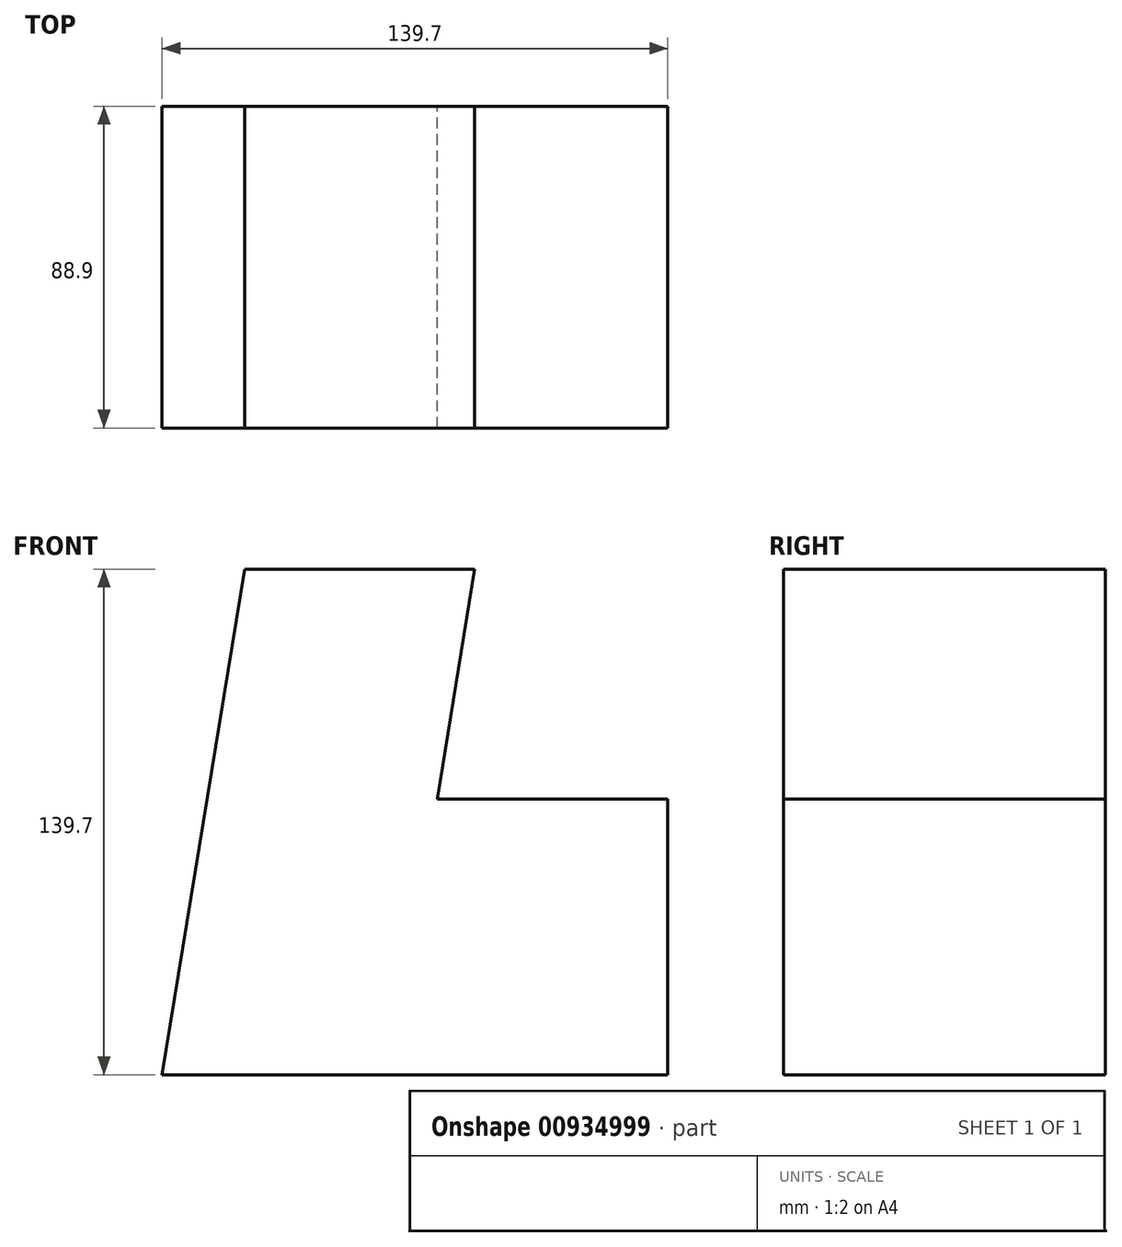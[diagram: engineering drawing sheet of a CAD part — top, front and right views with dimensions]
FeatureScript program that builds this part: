
annotation { "Feature Type Name" : "Feature", "Feature Type Description" : "" }
export const myFeature = defineFeature(function(context is Context, id is Id, definition is map)
    precondition{}
    {
        {
            var Q0;
            Q0=qCreatedBy(makeId("Front.planeOp"),FACE);
            var sketch = newSketch(context, id + "F0", { "sketchPlane" : qUnion([Q0])});
            skLineSegment(sketch, "E0", {"start": v(0, 0) * mm, "end": v(22.88, 139.7) * mm});
            skLineSegment(sketch, "E1", {"start": v(22.88, 139.7) * mm, "end": v(139.7, 139.7) * mm});
            skLineSegment(sketch, "E2", {"start": v(139.7, 139.7) * mm, "end": v(139.7, 0) * mm});
            skLineSegment(sketch, "E3", {"start": v(139.7, 0) * mm, "end": v(0, 0) * mm});
            skSolve(sketch);
        }
        {
            var Q0;
            Q0 = qSketchRegion(id + "F0", true);
            extrude(context, id + "F1", {"entities" : qUnion([Q0]), "depth" : 88.9 * mm, "offsetDistance" : 25.4 * mm});
        }
        {
            var Q0;
            Q0=qCreatedBy(makeId("Front.planeOp"),FACE);
            var sketch = newSketch(context, id + "F2", { "sketchPlane" : qUnion([Q0])});
            skLineSegment(sketch, "E4", {"start": v(139.7, 139.7) * mm, "end": v(86.38, 139.7) * mm});
            skLineSegment(sketch, "E5", {"start": v(86.38, 139.7) * mm, "end": v(75.98, 76.2) * mm});
            skLineSegment(sketch, "E6", {"start": v(75.98, 76.2) * mm, "end": v(139.7, 76.2) * mm});
            skLineSegment(sketch, "E7", {"start": v(139.7, 76.2) * mm, "end": v(139.7, 139.7) * mm});
            skSolve(sketch);
        }
        {
            var Q0;
            Q0 = qSketchRegion(id + "F2", true);
            extrude(context, id + "F3", {"entities" : qUnion([Q0]), "operationType" : NewBodyOperationType.REMOVE, "depth" : 254 * mm, "offsetDistance" : 25.4 * mm, "symmetric" : true});
        }
    });
